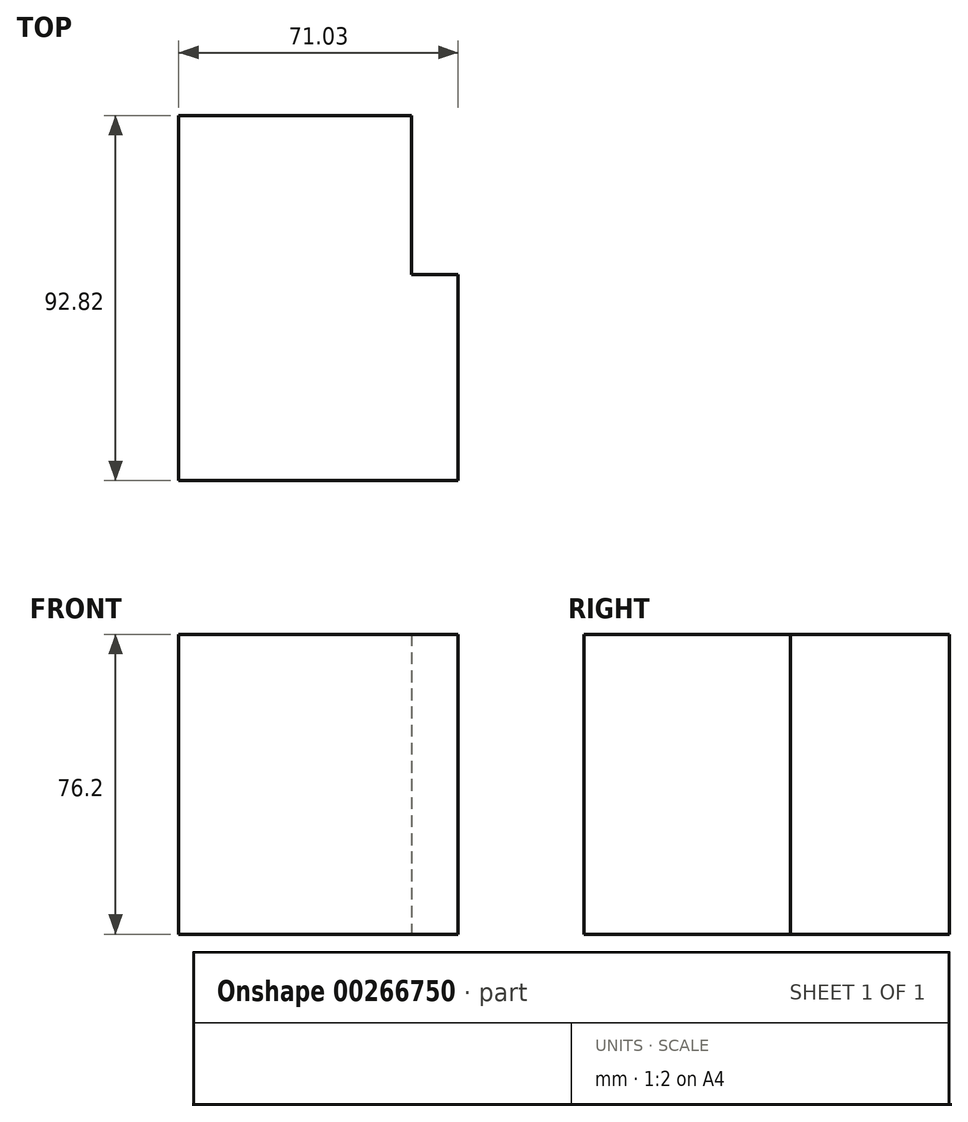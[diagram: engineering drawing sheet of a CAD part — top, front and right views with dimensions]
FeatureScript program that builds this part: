
annotation { "Feature Type Name" : "Feature", "Feature Type Description" : "" }
export const myFeature = defineFeature(function(context is Context, id is Id, definition is map)
    precondition{}
    {
        {
            var Q0;
            Q0=qCreatedBy(makeId("Top.planeOp"),FACE);
            var sketch = newSketch(context, id + "F0", { "sketchPlane" : qUnion([Q0])});
            skLineSegment(sketch, "E0.bottom", {"start": v(0, 0) * mm, "end": v(59.17, 0) * mm});
            skLineSegment(sketch, "E0.top", {"start": v(0, 40.4) * mm, "end": v(59.17, 40.4) * mm});
            skLineSegment(sketch, "E0.left", {"start": v(0, 0) * mm, "end": v(0, 40.4) * mm});
            skLineSegment(sketch, "E0.right", {"start": v(59.17, 0) * mm, "end": v(59.17, 40.4) * mm});
            skLineSegment(sketch, "E1.bottom", {"start": v(0, 0) * mm, "end": v(71.03, 0) * mm});
            skLineSegment(sketch, "E1.top", {"start": v(0, -52.42) * mm, "end": v(71.03, -52.42) * mm});
            skLineSegment(sketch, "E1.left", {"start": v(0, 0) * mm, "end": v(0, -52.42) * mm});
            skLineSegment(sketch, "E1.right", {"start": v(71.03, 0) * mm, "end": v(71.03, -52.42) * mm});
            skSolve(sketch);
        }
        {
            var Q0;
            Q0=makeQuery(id+"F0.imprint","IMPRINT",FACE,{"disambiguationData":[TD([[makeQuery(id+"F0.imprint","IMPRINT",EDGE,{"derivedFrom":sQuery(id+"F0.wireOp",EDGE,"E0.top")}),-1.0]])]});
            var Q1;
            Q1=makeQuery(id+"F0.imprint","IMPRINT",FACE,{"disambiguationData":[TD([[makeQuery(id+"F0.imprint","IMPRINT",EDGE,{"derivedFrom":sQuery(id+"F0.wireOp",EDGE,"E1.top")}),1.0]])]});
            extrude(context, id + "F1", {"entities" : qUnion([Q0, Q1]), "endBound" : BoundingType.SYMMETRIC, "depth" : 76.2 * mm});
        }
    });
